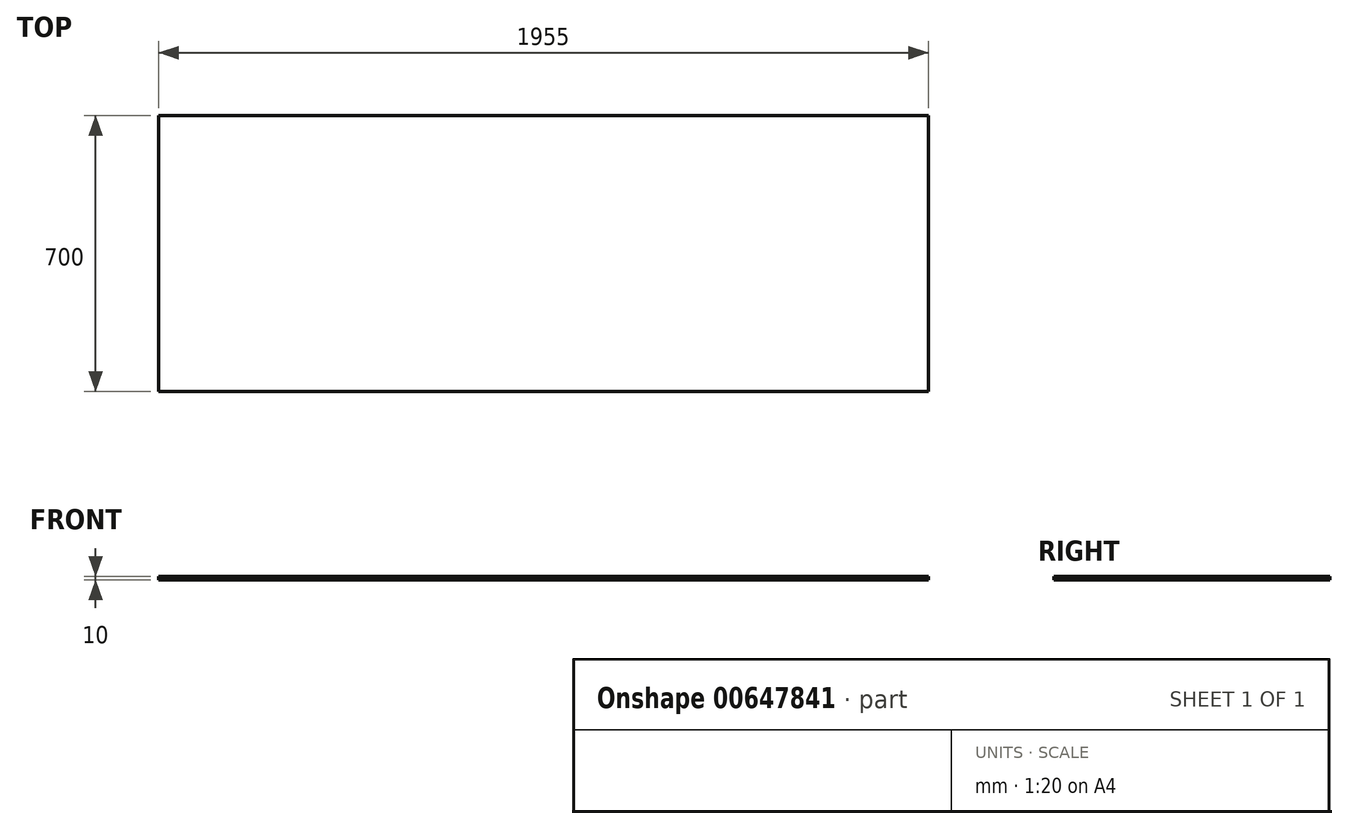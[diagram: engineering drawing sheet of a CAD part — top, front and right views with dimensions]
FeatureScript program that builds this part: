
annotation { "Feature Type Name" : "Feature", "Feature Type Description" : "" }
export const myFeature = defineFeature(function(context is Context, id is Id, definition is map)
    precondition{}
    {
        {
            var Q0;
            Q0=qCreatedBy(makeId("Top.planeOp"),FACE);
            var sketch = newSketch(context, id + "F0", { "sketchPlane" : qUnion([Q0])});
            skLineSegment(sketch, "E0.bottom", {"start": v(977.5, -350) * mm, "end": v(-977.5, -350) * mm});
            skLineSegment(sketch, "E0.top", {"start": v(977.5, 350) * mm, "end": v(-977.5, 350) * mm});
            skLineSegment(sketch, "E0.left", {"start": v(977.5, -350) * mm, "end": v(977.5, 350) * mm});
            skLineSegment(sketch, "E0.right", {"start": v(-977.5, -350) * mm, "end": v(-977.5, 350) * mm});
            skPoint(sketch, "E0.middle", {"position": v(0, 0) * mm});
            skSolve(sketch);
        }
        {
            var Q0;
            Q0=makeQuery(id+"F0.imprint","IMPRINT",FACE,{"disambiguationData":[TD([[makeQuery(id+"F0.imprint","IMPRINT",EDGE,{"derivedFrom":sQuery(id+"F0.wireOp",EDGE,"E0.bottom")}),-1.0]])]});
            extrude(context, id + "F1", {"entities" : qUnion([Q0]), "depth" : 10 * mm, "offsetDistance" : 25 * mm});
        }
    });
